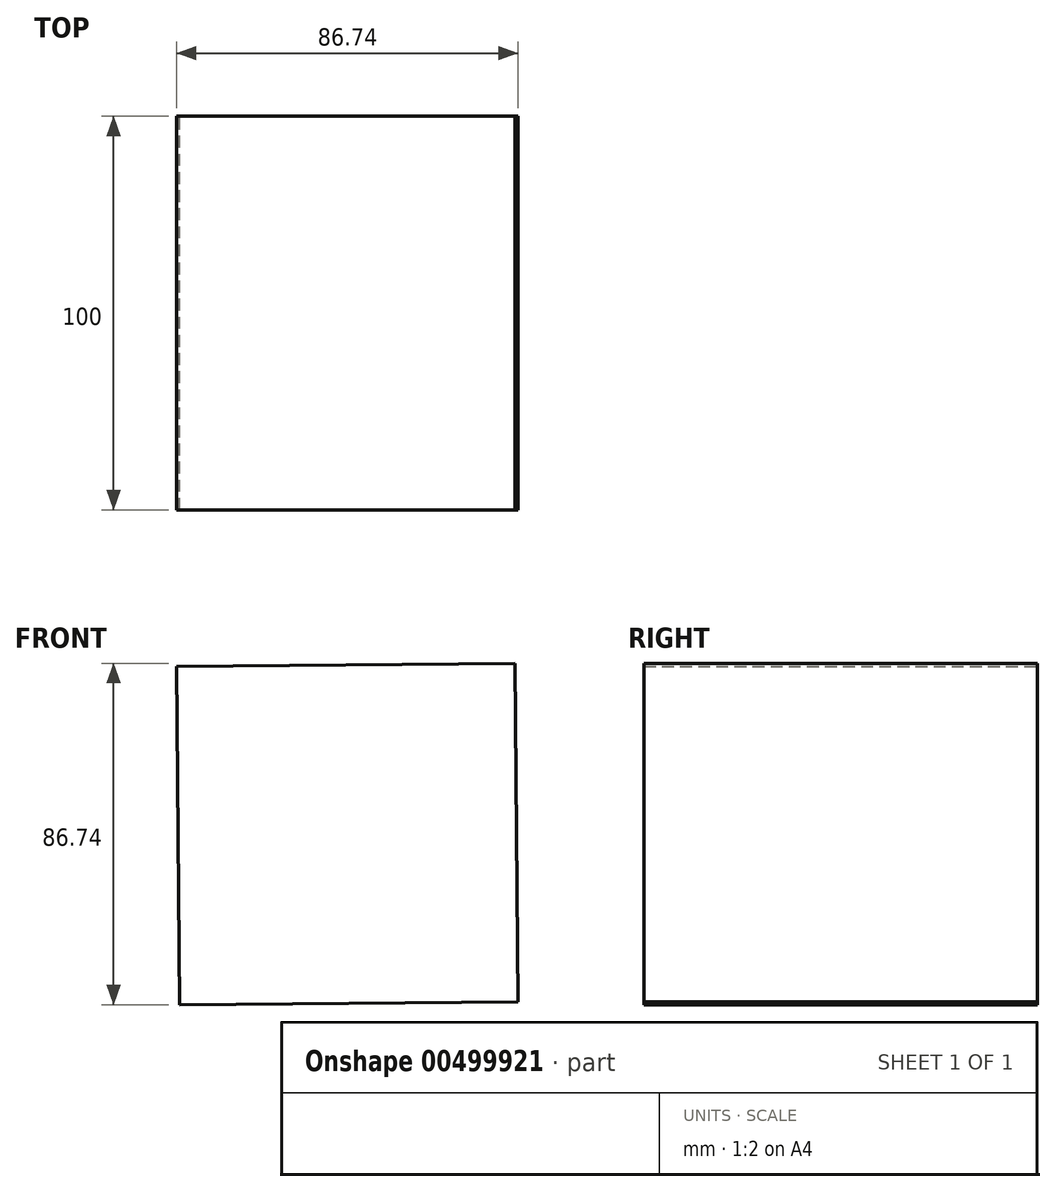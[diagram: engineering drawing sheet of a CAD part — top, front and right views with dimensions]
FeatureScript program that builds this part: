
annotation { "Feature Type Name" : "Feature", "Feature Type Description" : "" }
export const myFeature = defineFeature(function(context is Context, id is Id, definition is map)
    precondition{}
    {
        {
            var Q0;
            Q0=qCreatedBy(makeId("Front.planeOp"),FACE);
            var sketch = newSketch(context, id + "F0", { "sketchPlane" : qUnion([Q0])});
            skCircle(sketch, "E0.cCircle", {"center": v(0, 0) * mm, "radius": 60.8 * mm, "construction": true});
            skLineSegment(sketch, "E0.0", {"start": v(42.62, 43.37) * mm, "end": v(43.37, -42.62) * mm});
            skLineSegment(sketch, "E0.1", {"start": v(43.37, -42.62) * mm, "end": v(-42.62, -43.37) * mm});
            skLineSegment(sketch, "E0.2", {"start": v(-42.62, -43.37) * mm, "end": v(-43.37, 42.62) * mm});
            skLineSegment(sketch, "E0.3", {"start": v(-43.37, 42.62) * mm, "end": v(42.62, 43.37) * mm});
            skSolve(sketch);
        }
        {
            var Q0;
            Q0=makeQuery(id+"F0.imprint","IMPRINT",FACE,{"disambiguationData":[TD([[makeQuery(id+"F0.imprint","IMPRINT",EDGE,{"derivedFrom":sQuery(id+"F0.wireOp",EDGE,"E0.0")}),-1.0]])]});
            extrude(context, id + "F1", {"entities" : qUnion([Q0]), "depth" : 100 * mm, "symmetric" : true});
        }
    });
